# Revit family: 4. Секция электрического нагревателя ANR E1
name_source: partatom
category: Оборудование
revit_build: Autodesk Revit 2016 (Build: 20151209_0715(x64)
units: mm (PartAtom-declared; Revit-internal decimal feet)

## family parameters
Всегда вертикально = Да
На основе рабочей плоскости = Нет
Общий = Нет
При загрузке вырезать с полостями = Нет
Размер круглого соединителя = Использовать диаметр
Тип детали = Нормальный
Точка расчета площади = Нет

## types (24) — shared parameters
h = 130 мм
Д = 575 мм
Д1 = 555 мм
Единица измерения = шт.
Завод изготовитель = KORF
Ключевая пометка = Вентиляция
Наименование и тех.хар-ка = Секция электрического нагревателя
Раздел = ОВ
Синий = Синий
высота ножек = 120 мм

## per-type parameters (varying)
| type | А | А1 | Б | Б1 | Высота | Материал | Мощность, кВт | Середина | Ширина |
| ANR 6 E1.30 | 1100 мм | 1080 мм | 1100 мм | 1080 мм | 1025 мм | RAL 0000 Серый металл | 30 Вт | 670 мм | 1025 мм |
| ANR 7 E1.30 | 1100 мм | 1080 мм | 1320 мм | 1300 мм | 1245 мм | Сталь серая | 30 Вт | 780 мм | 1025 мм |
| ANR 8 E1.30 | 1320 мм | 1300 мм | 1320 мм | 1300 мм | 1245 мм | Сталь серая | 30 Вт | 780 мм | 1245 мм |
| ANR 12 E1.30 | 1435 мм | 1415 мм | 1435 мм | 1415 мм | 1360 мм | Сталь серая | 30 Вт | 838 мм | 1360 мм |
| ANR 6 E1.45 | 1100 мм | 1080 мм | 1100 мм | 1080 мм | 1025 мм | Сталь серая | 45 Вт | 670 мм | 1025 мм |
| ANR 6 E1.60 | 1100 мм | 1080 мм | 1100 мм | 1080 мм | 1025 мм | Сталь серая | 60 Вт | 670 мм | 1025 мм |
| ANR 6 E1.75 | 1100 мм | 1080 мм | 1100 мм | 1080 мм | 1025 мм | Сталь серая | 75 Вт | 670 мм | 1025 мм |
| ANR 6 E1.90 | 1100 мм | 1080 мм | 1100 мм | 1080 мм | 1025 мм | Сталь серая | 90 Вт | 670 мм | 1025 мм |
| ANR 6 E1.120 | 1100 мм | 1080 мм | 1100 мм | 1080 мм | 1025 мм | Сталь серая | 120 Вт | 670 мм | 1025 мм |
| ANR 7 E1.45 | 1100 мм | 1080 мм | 1320 мм | 1300 мм | 1245 мм | Сталь серая | 45 Вт | 780 мм | 1025 мм |
| ANR 7 E1.60 | 1100 мм | 1080 мм | 1320 мм | 1300 мм | 1245 мм | Сталь серая | 60 Вт | 780 мм | 1025 мм |
| ANR 7 E1.75 | 1100 мм | 1080 мм | 1320 мм | 1300 мм | 1245 мм | Сталь серая | 75 Вт | 780 мм | 1025 мм |
| ANR 7 E1.90 | 1100 мм | 1080 мм | 1320 мм | 1300 мм | 1245 мм | Сталь серая | 90 Вт | 780 мм | 1025 мм |
| ANR 7 E1.120 | 1100 мм | 1080 мм | 1320 мм | 1300 мм | 1245 мм | Сталь серая | 120 Вт | 780 мм | 1025 мм |
| ANR 8 E1.45 | 1320 мм | 1300 мм | 1320 мм | 1300 мм | 1245 мм | Сталь серая | 45 Вт | 780 мм | 1245 мм |
| ANR 8 E1.60 | 1320 мм | 1300 мм | 1320 мм | 1300 мм | 1245 мм | Сталь серая | 60 Вт | 780 мм | 1245 мм |
| ANR 8 E1.75 | 1320 мм | 1300 мм | 1320 мм | 1300 мм | 1245 мм | Сталь серая | 75 Вт | 780 мм | 1245 мм |
| ANR 8 E1.90 | 1320 мм | 1300 мм | 1320 мм | 1300 мм | 1245 мм | Сталь серая | 90 Вт | 780 мм | 1245 мм |
| ANR 8 E1.120 | 1320 мм | 1300 мм | 1320 мм | 1300 мм | 1245 мм | Сталь серая | 120 Вт | 780 мм | 1245 мм |
| ANR 12 E1.45 | 1435 мм | 1415 мм | 1435 мм | 1415 мм | 1360 мм | Сталь серая | 45 Вт | 838 мм | 1360 мм |
| ANR 12 E1.60 | 1435 мм | 1415 мм | 1435 мм | 1415 мм | 1360 мм | Сталь серая | 60 Вт | 838 мм | 1360 мм |
| ANR 12 E1.75 | 1435 мм | 1415 мм | 1435 мм | 1415 мм | 1360 мм | Сталь серая | 75 Вт | 838 мм | 1360 мм |
| ANR 12 E1.90 | 1435 мм | 1415 мм | 1435 мм | 1415 мм | 1360 мм | Сталь серая | 90 Вт | 838 мм | 1360 мм |
| ANR 12 E1.120 | 1435 мм | 1415 мм | 1435 мм | 1415 мм | 1360 мм | Сталь серая | 120 Вт | 838 мм | 1360 мм |

note: column(s) folded — value = type name in every type: Тип, марка, обозначение
